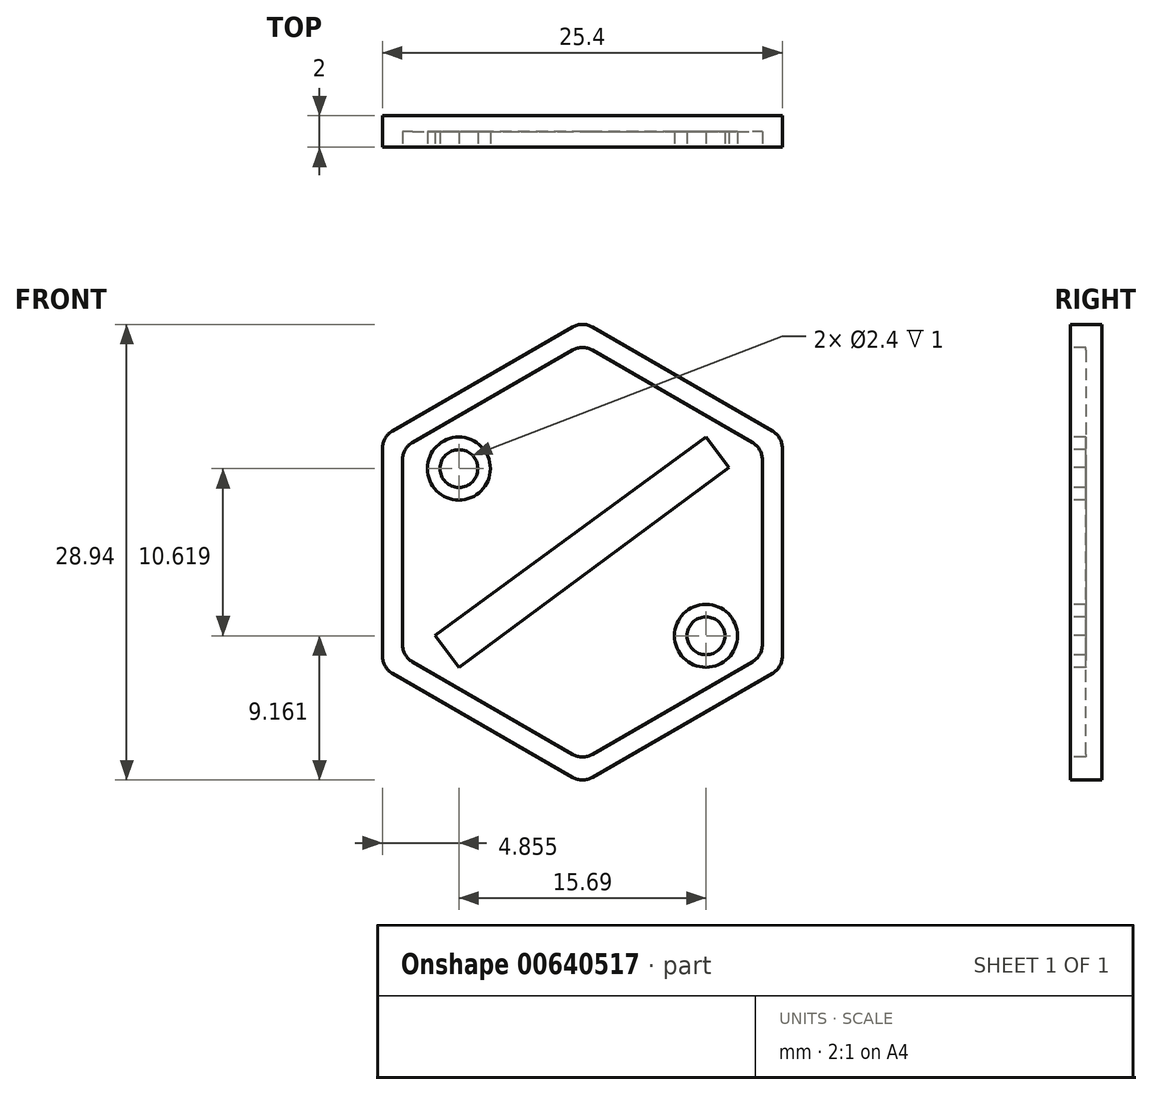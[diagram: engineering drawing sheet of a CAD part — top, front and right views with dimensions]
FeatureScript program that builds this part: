
annotation { "Feature Type Name" : "Feature", "Feature Type Description" : "" }
export const myFeature = defineFeature(function(context is Context, id is Id, definition is map)
    precondition{}
    {
        {
            var Q0;
            Q0=qCreatedBy(makeId("Front.planeOp"),FACE);
            var sketch = newSketch(context, id + "F0", { "sketchPlane" : qUnion([Q0])});
            skCircle(sketch, "E0.cCircle", {"center": v(0, 0) * mm, "radius": 12.7 * mm, "construction": true});
            skLineSegment(sketch, "E0.0", {"start": v(0.63, 14.3) * mm, "end": v(12.07, 7.7) * mm});
            skLineSegment(sketch, "E0.1", {"start": v(12.7, 6.6) * mm, "end": v(12.7, -6.6) * mm});
            skLineSegment(sketch, "E0.2", {"start": v(12.07, -7.7) * mm, "end": v(0.63, -14.3) * mm});
            skLineSegment(sketch, "E0.3", {"start": v(-0.63, -14.3) * mm, "end": v(-12.06, -7.7) * mm});
            skLineSegment(sketch, "E0.4", {"start": v(-12.7, -6.6) * mm, "end": v(-12.7, 6.6) * mm});
            skLineSegment(sketch, "E0.5", {"start": v(-12.07, 7.7) * mm, "end": v(-0.64, 14.3) * mm});
            skPoint(sketch, "E0.0.midPoint", {"position": v(6.35, 11) * mm});
            skPoint(sketch, "E1.visualSharp", {"position": v(0, 14.66) * mm});
            skArc(sketch, "E1.filletArc", {"start": v(0.63, 14.3) * mm, "mid": v(0, 14.47) * mm, "end": v(-0.64, 14.3) * mm});
            skPoint(sketch, "E2.visualSharp", {"position": v(-12.7, 7.33) * mm});
            skArc(sketch, "E2.filletArc", {"start": v(-12.07, 7.7) * mm, "mid": v(-12.53, 7.23) * mm, "end": v(-12.7, 6.6) * mm});
            skPoint(sketch, "E3.visualSharp", {"position": v(12.7, 7.33) * mm});
            skArc(sketch, "E3.filletArc", {"start": v(12.7, 6.6) * mm, "mid": v(12.53, 7.23) * mm, "end": v(12.07, 7.7) * mm});
            skPoint(sketch, "E4.visualSharp", {"position": v(12.7, -7.33) * mm});
            skArc(sketch, "E4.filletArc", {"start": v(12.07, -7.7) * mm, "mid": v(12.53, -7.23) * mm, "end": v(12.7, -6.6) * mm});
            skPoint(sketch, "E5.visualSharp", {"position": v(0, -14.66) * mm});
            skArc(sketch, "E5.filletArc", {"start": v(-0.63, -14.3) * mm, "mid": v(0, -14.47) * mm, "end": v(0.63, -14.3) * mm});
            skPoint(sketch, "E6.visualSharp", {"position": v(-12.7, -7.33) * mm});
            skArc(sketch, "E6.filletArc", {"start": v(-12.7, -6.6) * mm, "mid": v(-12.53, -7.23) * mm, "end": v(-12.06, -7.7) * mm});
            skSolve(sketch);
        }
        {
            var Q0;
            Q0 = qSketchRegion(id + "F0", true);
            extrude(context, id + "F1", {"entities" : qUnion([Q0]), "depth" : 2 * mm, "offsetDistance" : 25.4 * mm, "symmetric" : true});
        }
        {
            var Q0;
            Q0=makeQuery(id+"F1.opExtrude","CAP_FACE",FACE,{"disambiguationData":[OSD([sQuery(id+"F0.wireOp",EDGE,"E0.0"),sQuery(id+"F0.wireOp",EDGE,"E0.1"),sQuery(id+"F0.wireOp",EDGE,"E0.2"),sQuery(id+"F0.wireOp",EDGE,"E0.3"),sQuery(id+"F0.wireOp",EDGE,"E0.4"),sQuery(id+"F0.wireOp",EDGE,"E0.5")])],"isStart":false});
            var sketch = newSketch(context, id + "F2", { "sketchPlane" : qUnion([Q0])});
            skCircle(sketch, "E7", {"center": v(-7.85, 5.31) * mm, "radius": 2 * mm});
            skCircle(sketch, "E8.MirrorC", {"center": v(7.85, -5.31) * mm, "radius": 2 * mm});
            skLineSegment(sketch, "E9", {"start": v(-7.85, -7.33) * mm, "end": v(-9.36, -5.3) * mm});
            skLineSegment(sketch, "E10", {"start": v(-9.36, -5.3) * mm, "end": v(7.85, 7.33) * mm});
            skLineSegment(sketch, "E11", {"start": v(7.85, 7.33) * mm, "end": v(9.3, 5.36) * mm});
            skLineSegment(sketch, "E12", {"start": v(9.3, 5.36) * mm, "end": v(-7.85, -7.33) * mm});
            skSolve(sketch);
        }
        {
            var Q0;
            Q0=makeQuery(id+"F2.imprint","IMPRINT",FACE,{"disambiguationData":[TD([[makeQuery(id+"F2.imprint","IMPRINT",EDGE,{"derivedFrom":sQuery(id+"F2.wireOp",EDGE,"E7")}),-1.0]])]});
            var sketch = newSketch(context, id + "F3", { "sketchPlane" : qUnion([Q0])});
            skCircle(sketch, "E13.cCircle", {"center": v(0, 0) * mm, "radius": 11.43 * mm, "construction": true});
            skLineSegment(sketch, "E13.0", {"start": v(0.64, 12.83) * mm, "end": v(10.8, 6.97) * mm});
            skLineSegment(sketch, "E13.1", {"start": v(11.43, 5.87) * mm, "end": v(11.43, -5.87) * mm});
            skLineSegment(sketch, "E13.2", {"start": v(10.8, -6.97) * mm, "end": v(0.64, -12.83) * mm});
            skLineSegment(sketch, "E13.3", {"start": v(-0.64, -12.83) * mm, "end": v(-10.8, -6.97) * mm});
            skLineSegment(sketch, "E13.4", {"start": v(-11.43, -5.87) * mm, "end": v(-11.43, 5.87) * mm});
            skLineSegment(sketch, "E13.5", {"start": v(-10.8, 6.97) * mm, "end": v(-0.64, 12.83) * mm});
            skPoint(sketch, "E13.0.midPoint", {"position": v(5.71, 9.9) * mm});
            skPoint(sketch, "E14.visualSharp", {"position": v(0, 13.2) * mm});
            skArc(sketch, "E14.filletArc", {"start": v(0.64, 12.83) * mm, "mid": v(0, 13) * mm, "end": v(-0.63, 12.83) * mm});
            skPoint(sketch, "E15.visualSharp", {"position": v(-11.43, 6.6) * mm});
            skArc(sketch, "E15.filletArc", {"start": v(-10.8, 6.97) * mm, "mid": v(-11.26, 6.5) * mm, "end": v(-11.43, 5.87) * mm});
            skPoint(sketch, "E16.visualSharp", {"position": v(11.43, 6.6) * mm});
            skArc(sketch, "E16.filletArc", {"start": v(11.43, 5.87) * mm, "mid": v(11.26, 6.5) * mm, "end": v(10.8, 6.97) * mm});
            skPoint(sketch, "E17.visualSharp", {"position": v(11.43, -6.6) * mm});
            skArc(sketch, "E17.filletArc", {"start": v(10.8, -6.97) * mm, "mid": v(11.26, -6.5) * mm, "end": v(11.43, -5.87) * mm});
            skPoint(sketch, "E18.visualSharp", {"position": v(0, -13.2) * mm});
            skArc(sketch, "E18.filletArc", {"start": v(-0.64, -12.83) * mm, "mid": v(0, -13) * mm, "end": v(0.64, -12.83) * mm});
            skPoint(sketch, "E19.visualSharp", {"position": v(-11.43, -6.6) * mm});
            skArc(sketch, "E19.filletArc", {"start": v(-11.43, -5.87) * mm, "mid": v(-11.26, -6.5) * mm, "end": v(-10.8, -6.97) * mm});
            skSolve(sketch);
        }
        {
            var Q0;
            Q0 = qSketchRegion(id + "F3", true);
            extrude(context, id + "F4", {"entities" : qUnion([Q0]), "operationType" : NewBodyOperationType.REMOVE, "oppositeDirection" : true, "depth" : 1 * mm, "offsetDistance" : 25.4 * mm});
        }
        {
            var Q0;
            Q0=makeQuery(id+"F2.imprint","IMPRINT",FACE,{"disambiguationData":[TD([[makeQuery(id+"F2.imprint","IMPRINT",EDGE,{"derivedFrom":sQuery(id+"F2.wireOp",EDGE,"E7")}),-1.0]])]});
            var sketch = newSketch(context, id + "F5", { "sketchPlane" : qUnion([Q0])});
            skCircle(sketch, "E20", {"center": v(-7.84, 5.3) * mm, "radius": 1.2 * mm});
            skCircle(sketch, "E21.MirrorC", {"center": v(7.84, -5.3) * mm, "radius": 1.2 * mm});
            skSolve(sketch);
        }
        {
            var Q0;
            Q0 = qSketchRegion(id + "F2", true);
            extrude(context, id + "F6", {"entities" : qUnion([Q0]), "operationType" : NewBodyOperationType.ADD, "oppositeDirection" : true, "depth" : 1 * mm, "offsetDistance" : 25.4 * mm});
        }
        {
            var Q0;
            Q0 = qSketchRegion(id + "F5", true);
            extrude(context, id + "F7", {"entities" : qUnion([Q0]), "operationType" : NewBodyOperationType.REMOVE, "oppositeDirection" : true, "depth" : 1 * mm, "offsetDistance" : 25.4 * mm});
        }
    });
